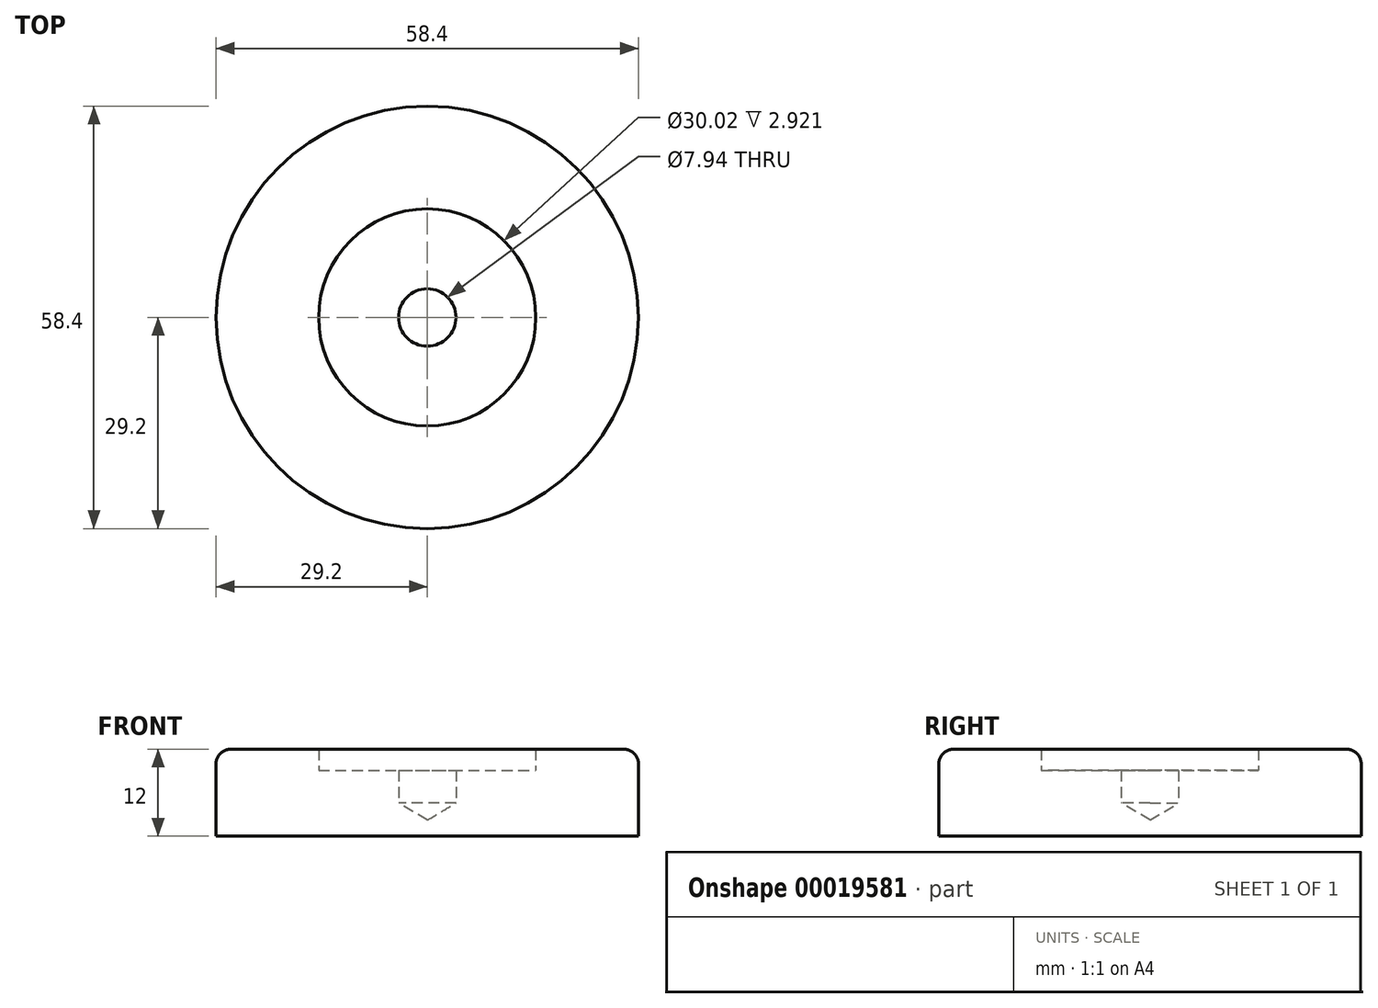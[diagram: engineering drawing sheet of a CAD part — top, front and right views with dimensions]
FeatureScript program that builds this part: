
annotation { "Feature Type Name" : "Feature", "Feature Type Description" : "" }
export const myFeature = defineFeature(function(context is Context, id is Id, definition is map)
    precondition{}
    {
        {
            var Q0;
            Q0=qCreatedBy(makeId("Front.planeOp"),FACE);
            var sketch = newSketch(context, id + "F0", { "sketchPlane" : qUnion([Q0])});
            skLineSegment(sketch, "E0", {"start": v(0, 0) * mm, "end": v(0, 9.08) * mm});
            skLineSegment(sketch, "E1", {"start": v(0, 9.08) * mm, "end": v(15.01, 9.08) * mm});
            skLineSegment(sketch, "E2", {"start": v(15.01, 9.08) * mm, "end": v(15.01, 12) * mm});
            skLineSegment(sketch, "E3", {"start": v(15.01, 12) * mm, "end": v(21.71, 12) * mm});
            skLineSegment(sketch, "E4", {"start": v(21.71, 12) * mm, "end": v(29.2, 12) * mm});
            skLineSegment(sketch, "E5", {"start": v(29.2, 12) * mm, "end": v(29.2, 0) * mm});
            skLineSegment(sketch, "E6", {"start": v(29.2, 0) * mm, "end": v(0, 0) * mm});
            skLineSegment(sketch, "E7", {"start": v(0, 0) * mm, "end": v(0, 42.63) * mm, "construction": true});
            skSolve(sketch);
        }
        {
            var Q0;
            Q0 = qSketchRegion(id + "F0", true);
            var Q1;
            Q1=sQuery(id+"F0.wireOp",EDGE,"E7");
            revolve(context, id + "F1", {"surfaceOperationType" : NewSurfaceOperationType.NEW, "entities" : qUnion([Q0]), "axis" : qUnion([Q1]), "revolveType" : RevolveType.FULL});
        }
        {
            var Q0;
            Q0=makeQuery(id+"F1.opRevolve","SWEPT_FACE",FACE,{"disambiguationData":[OSD([sQuery(id+"F0.wireOp",EDGE,"E1")])]});
            var sketch = newSketch(context, id + "F2", { "sketchPlane" : qUnion([Q0])});
            skPoint(sketch, "E8", {"position": v(0, 0) * mm});
            skSolve(sketch);
        }
        {
            var Q0;
            Q0=sQuery(id+"F2.wireOp",VERTEX,"E8");
            var Q1;
            Q1=makeQuery(id+"F1.opRevolve","SWEPT_BODY",BODY,{"disambiguationData":[OSD([sQuery(id+"F0.wireOp",EDGE,"E0"),sQuery(id+"F0.wireOp",EDGE,"E1"),sQuery(id+"F0.wireOp",EDGE,"E2"),sQuery(id+"F0.wireOp",EDGE,"E3"),sQuery(id+"F0.wireOp",EDGE,"E4"),sQuery(id+"F0.wireOp",EDGE,"E5"),sQuery(id+"F0.wireOp",EDGE,"E6")])]});
            hole(context, id + "F3", {"style" : HoleStyle.SIMPLE, "endStyle" : HoleEndStyle.BLIND, "standardTappedOrClearance" : lookupTablePath({ "standard" : "ANSI", "engagement" : "75%", "pitch" : "16 tpi", "size" : "3/8", "type" : "Tapped" }), "standardBlindInLast" : lookupTablePath({ "standard" : "ANSI", "engagement" : "75%", "pitch" : "16 tpi", "size" : "3/8", "type" : "Tapped" }), "holeDiameter" : 7.94 * mm, "holeDepth" : 4.5 * mm, "locations" : qUnion([Q0]), "scope" : qUnion([Q1]), "tappedDepth" : 1.24 * mm, "tapClearance" : 3, "majorDiameter" : 9.53 * mm, "showTappedDepth" : true, "startStyle" : HoleStartStyle.SKETCH});
        }
        {
            var Q0;
            Q0=makeQuery(id+"F1.opRevolve","SWEPT_EDGE",EDGE,{"disambiguationData":[OSD([sQuery(id+"F0.wireOp",EDGE,"E4"),sQuery(id+"F0.wireOp",EDGE,"E5")])]});
            fillet(context, id + "F4", {"entities" : qUnion([Q0]), "radius" : 2 * mm, "tangentPropagation" : true, "allowEdgeOverflow" : false});
        }
    });
